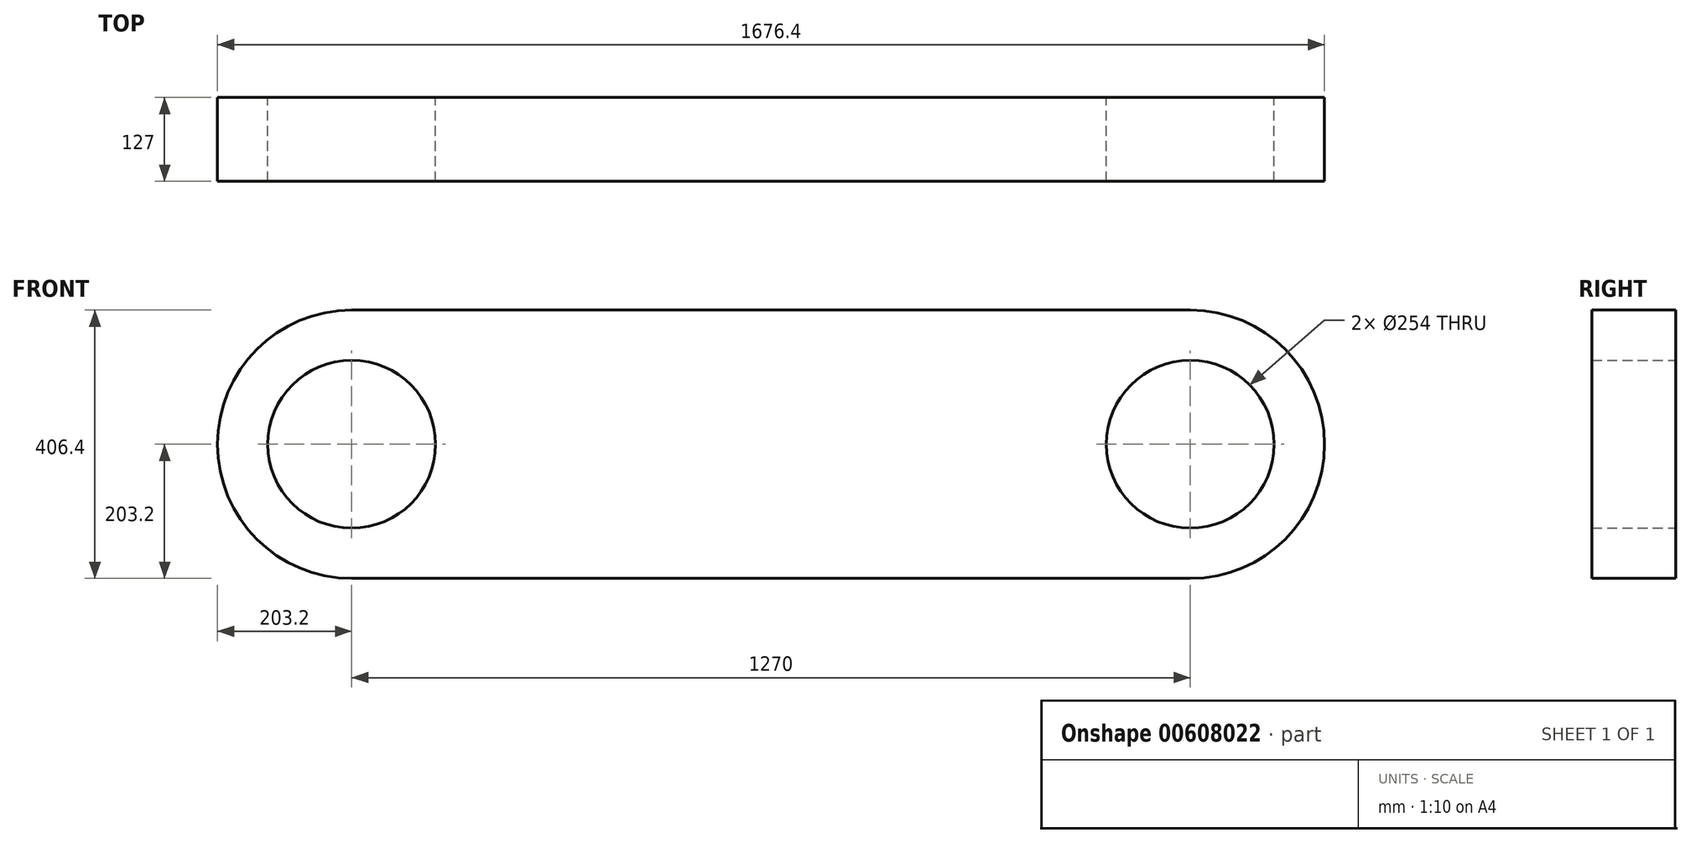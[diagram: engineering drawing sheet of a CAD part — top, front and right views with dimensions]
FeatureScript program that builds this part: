
annotation { "Feature Type Name" : "Feature", "Feature Type Description" : "" }
export const myFeature = defineFeature(function(context is Context, id is Id, definition is map)
    precondition{}
    {
        {
            var Q0;
            Q0=qCreatedBy(makeId("Front.planeOp"),FACE);
            var sketch = newSketch(context, id + "F0", { "sketchPlane" : qUnion([Q0])});
            skLineSegment(sketch, "E0.bottom", {"start": v(-635, 203.2) * mm, "end": v(635, 203.2) * mm});
            skLineSegment(sketch, "E0.top", {"start": v(-635, -203.2) * mm, "end": v(635, -203.2) * mm});
            skArc(sketch, "E1", {"start": v(-635, 203.2) * mm, "mid": v(-838.2, 0) * mm, "end": v(-635, -203.2) * mm});
            skArc(sketch, "E2", {"start": v(635, -203.2) * mm, "mid": v(838.2, 0) * mm, "end": v(635, 203.2) * mm});
            skCircle(sketch, "E3", {"center": v(635, 0) * mm, "radius": 127 * mm});
            skCircle(sketch, "E4", {"center": v(-635, 0) * mm, "radius": 127 * mm});
            skSolve(sketch);
        }
        {
            var Q0;
            Q0 = qSketchRegion(id + "F0", true);
            extrude(context, id + "F1", {"entities" : qUnion([Q0]), "endBound" : BoundingType.SYMMETRIC, "depth" : 127 * mm, "offsetDistance" : 25.4 * mm});
        }
    });
